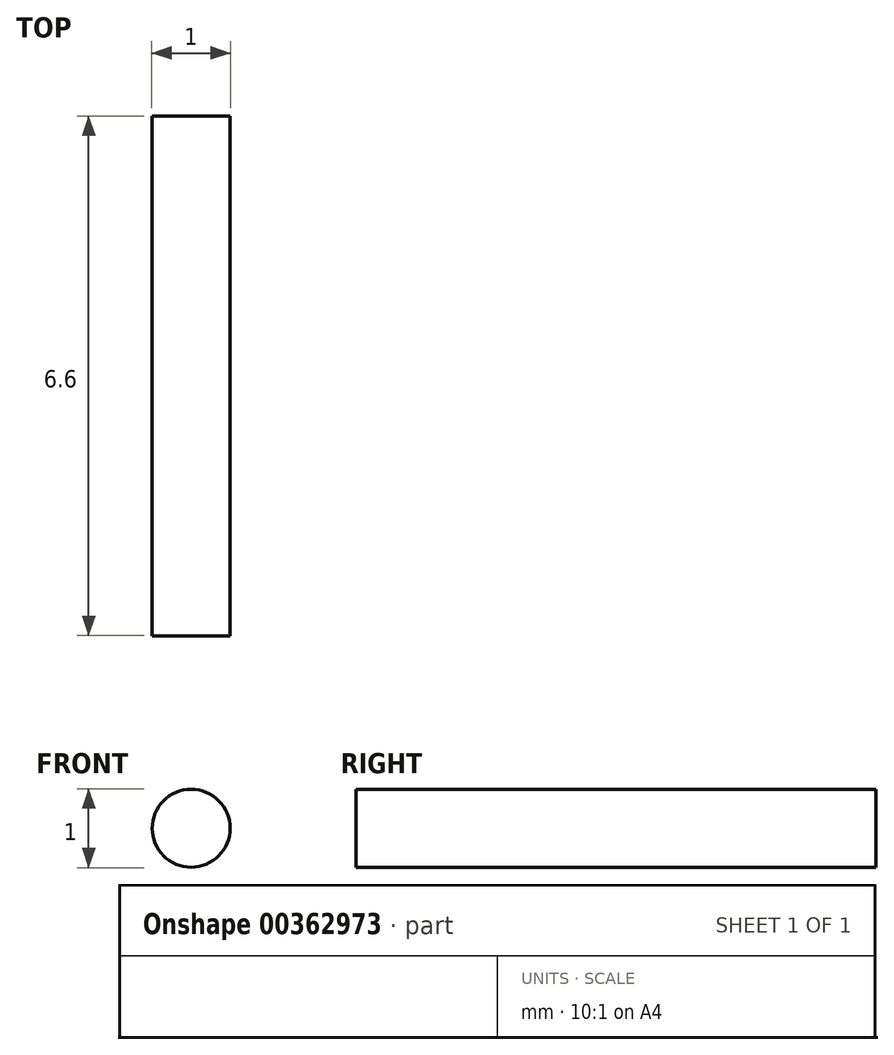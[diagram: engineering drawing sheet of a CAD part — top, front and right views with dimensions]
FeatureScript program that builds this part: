
annotation { "Feature Type Name" : "Feature", "Feature Type Description" : "" }
export const myFeature = defineFeature(function(context is Context, id is Id, definition is map)
    precondition{}
    {
        {
            var Q0;
            Q0=qCreatedBy(makeId("Front.planeOp"),FACE);
            var sketch = newSketch(context, id + "F0", { "sketchPlane" : qUnion([Q0])});
            skCircle(sketch, "E0", {"center": v(0, 0) * mm, "radius": 0.5 * mm});
            skSolve(sketch);
        }
        {
            var Q0;
            Q0=makeQuery(id+"F0.imprint","IMPRINT",FACE,{"disambiguationData":[TD([[makeQuery(id+"F0.imprint","IMPRINT",EDGE,{"derivedFrom":sQuery(id+"F0.wireOp",EDGE,"E0")}),1.0]])]});
            extrude(context, id + "F1", {"entities" : qUnion([Q0]), "depth" : 6.6 * mm});
        }
    });
